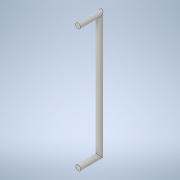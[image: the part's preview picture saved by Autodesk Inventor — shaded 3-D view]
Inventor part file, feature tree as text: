
AUTODESK INVENTOR PART (.ipt)
format: ipt  version: 2020 (Build 240168000, 168)  size: 102,400 bytes
history: native  units: mm
features: sketch x2, thicken_offset x2, plane x1, sweep x1
ambient origin geometry x8: Origin, YZ Plane, XZ Plane, XY Plane, X Axis, Y Axis, Z Axis, Center Point
bodies: Solid1 (feature_tree)
feature tree (6):
  sketch  "Sketch1"  dims[d3=0.0mm d4=0.0mm d6=25.0mm]
  plane  "Work Plane1"
  sweep  "Sweep1"
  thicken_offset  "Thicken1"
  thicken_offset  "Thicken2"
  sketch  "Sketch2"  dims[d8=25.0mm]
